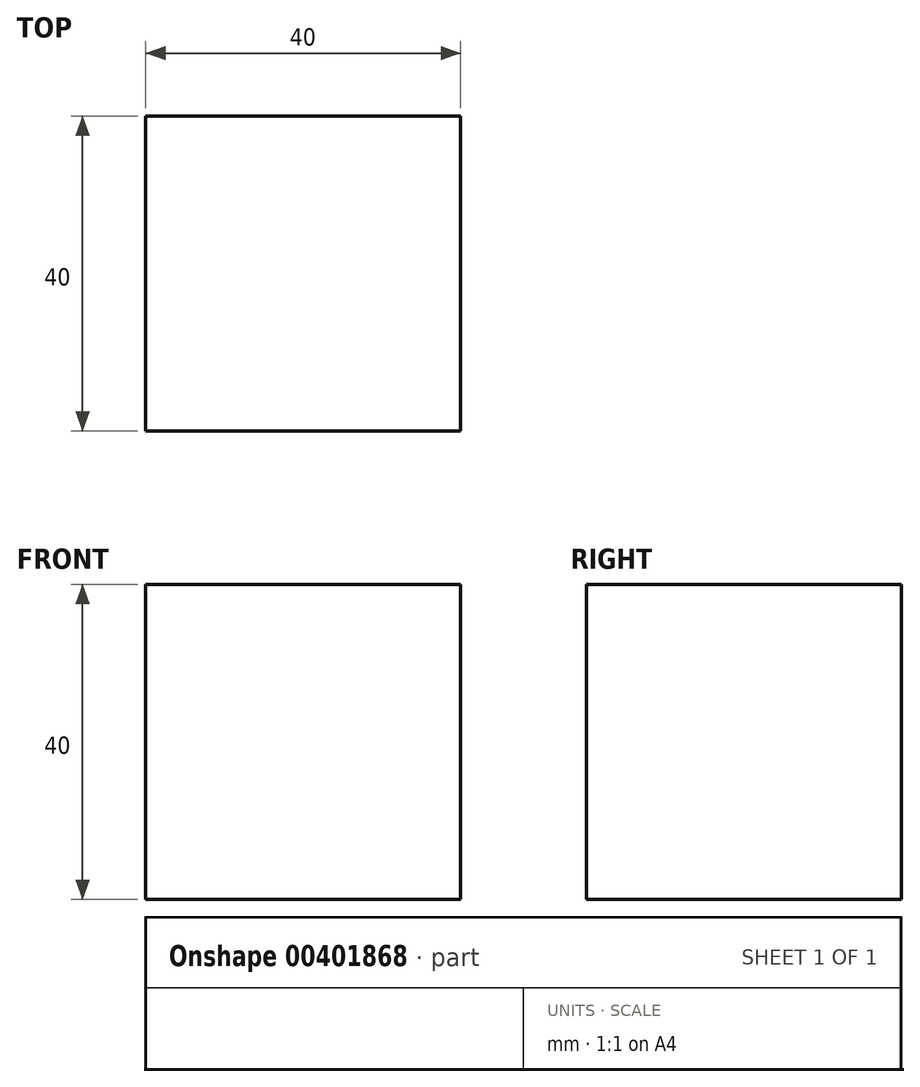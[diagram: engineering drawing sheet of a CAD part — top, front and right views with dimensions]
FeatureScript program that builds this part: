
annotation { "Feature Type Name" : "Feature", "Feature Type Description" : "" }
export const myFeature = defineFeature(function(context is Context, id is Id, definition is map)
    precondition{}
    {
        {
            var Q0;
            Q0=qCreatedBy(makeId("Top.planeOp"),FACE);
            var sketch = newSketch(context, id + "F0", { "sketchPlane" : qUnion([Q0])});
            skLineSegment(sketch, "E0.bottom", {"start": v(20, -20) * mm, "end": v(-20, -20) * mm});
            skLineSegment(sketch, "E0.top", {"start": v(20, 20) * mm, "end": v(-20, 20) * mm});
            skLineSegment(sketch, "E0.left", {"start": v(20, -20) * mm, "end": v(20, 20) * mm});
            skLineSegment(sketch, "E0.right", {"start": v(-20, -20) * mm, "end": v(-20, 20) * mm});
            skPoint(sketch, "E0.middle", {"position": v(0, 0) * mm});
            skSolve(sketch);
        }
        {
            var Q0;
            Q0 = qSketchRegion(id + "F0", true);
            extrude(context, id + "F1", {"entities" : qUnion([Q0]), "depth" : 40 * mm});
        }
    });
